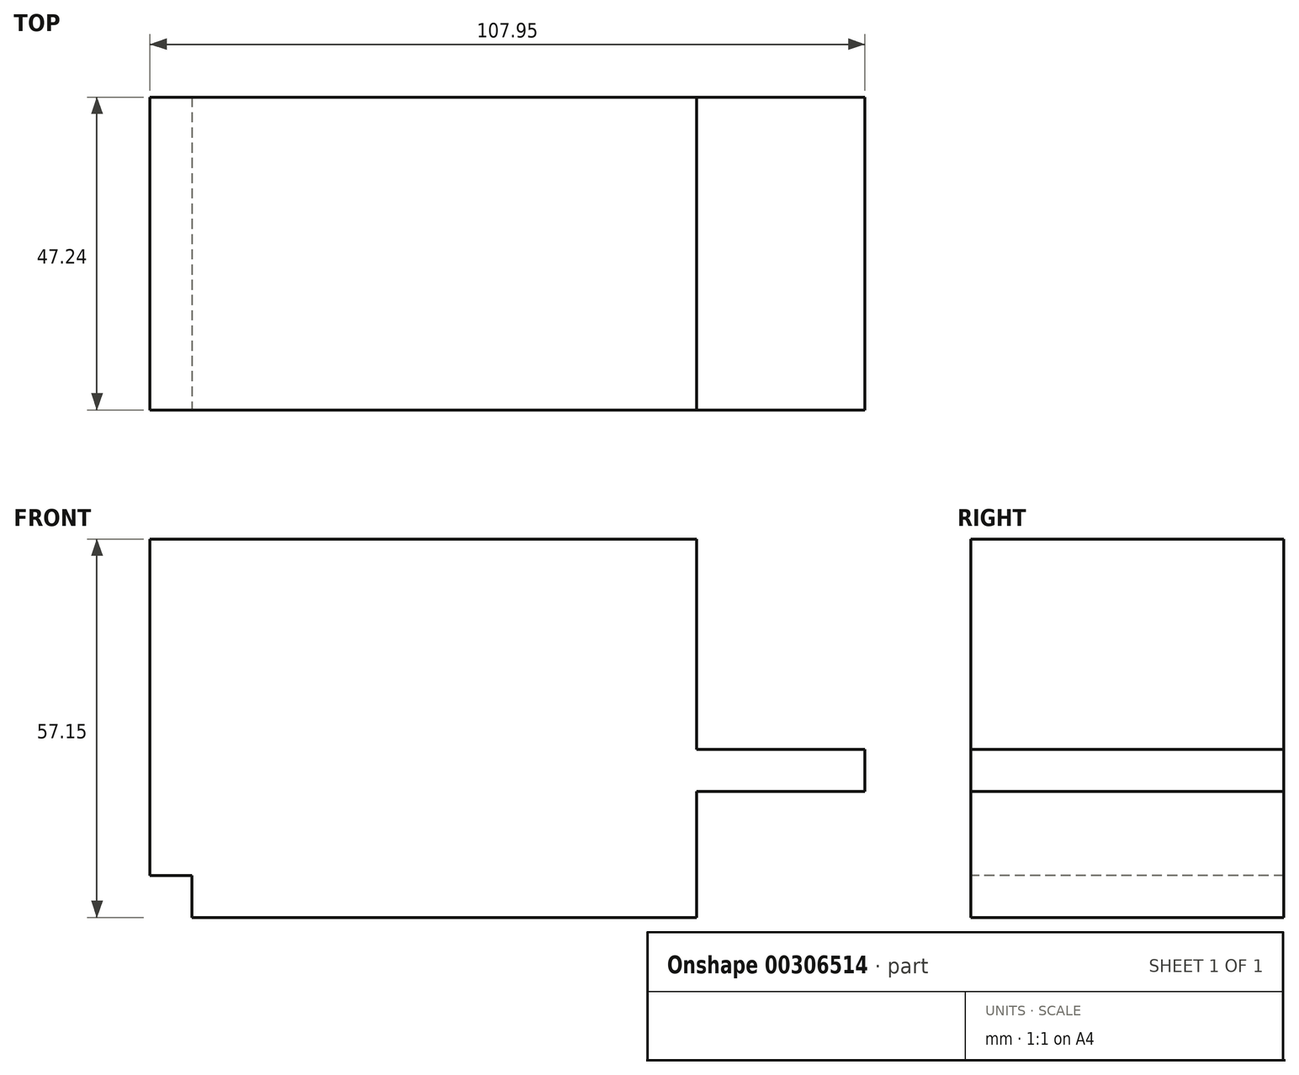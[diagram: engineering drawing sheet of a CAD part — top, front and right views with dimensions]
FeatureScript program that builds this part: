
annotation { "Feature Type Name" : "Feature", "Feature Type Description" : "" }
export const myFeature = defineFeature(function(context is Context, id is Id, definition is map)
    precondition{}
    {
        {
            var Q0;
            Q0=qCreatedBy(makeId("Front.planeOp"),FACE);
            var sketch = newSketch(context, id + "F0", { "sketchPlane" : qUnion([Q0])});
            skLineSegment(sketch, "E0", {"start": v(-29.7, 44.45) * mm, "end": v(-29.7, -6.35) * mm});
            skLineSegment(sketch, "E1", {"start": v(-29.7, -6.35) * mm, "end": v(-23.35, -6.35) * mm});
            skLineSegment(sketch, "E2", {"start": v(-23.35, -6.35) * mm, "end": v(-23.35, -12.7) * mm});
            skLineSegment(sketch, "E3", {"start": v(-23.35, -12.7) * mm, "end": v(52.85, -12.7) * mm});
            skLineSegment(sketch, "E4", {"start": v(52.85, -12.7) * mm, "end": v(52.85, 6.35) * mm});
            skLineSegment(sketch, "E5", {"start": v(52.85, 6.35) * mm, "end": v(78.25, 6.35) * mm});
            skLineSegment(sketch, "E6", {"start": v(78.25, 6.35) * mm, "end": v(78.25, 12.7) * mm});
            skLineSegment(sketch, "E7", {"start": v(78.25, 12.7) * mm, "end": v(52.85, 12.7) * mm});
            skLineSegment(sketch, "E8", {"start": v(52.85, 12.7) * mm, "end": v(52.85, 44.45) * mm});
            skLineSegment(sketch, "E9", {"start": v(52.85, 44.45) * mm, "end": v(-29.7, 44.45) * mm});
            skSolve(sketch);
        }
        {
            var Q0;
            Q0=makeQuery(id+"F0.imprint","IMPRINT",FACE,{"disambiguationData":[TD([[makeQuery(id+"F0.imprint","IMPRINT",EDGE,{"derivedFrom":sQuery(id+"F0.wireOp",EDGE,"E0")}),1.0]])]});
            extrude(context, id + "F1", {"entities" : qUnion([Q0]), "depth" : 25.4 * mm});
        }
        {
            var Q0;
            Q0=makeQuery(id+"F1.opExtrude","CAP_FACE",FACE,{"disambiguationData":[OSD([sQuery(id+"F0.wireOp",EDGE,"E0"),sQuery(id+"F0.wireOp",EDGE,"E1"),sQuery(id+"F0.wireOp",EDGE,"E2"),sQuery(id+"F0.wireOp",EDGE,"E3"),sQuery(id+"F0.wireOp",EDGE,"E4"),sQuery(id+"F0.wireOp",EDGE,"E5"),sQuery(id+"F0.wireOp",EDGE,"E6"),sQuery(id+"F0.wireOp",EDGE,"E7"),sQuery(id+"F0.wireOp",EDGE,"E8"),sQuery(id+"F0.wireOp",EDGE,"E9")])],"isStart":true});
            extrude(context, id + "F2", {"entities" : qUnion([Q0]), "operationType" : NewBodyOperationType.ADD, "depth" : 25.4 * mm});
        }
        {
            var Q0;
            Q0=makeQuery(id+"F1.opExtrude","CAP_FACE",FACE,{"disambiguationData":[OSD([sQuery(id+"F0.wireOp",EDGE,"E0"),sQuery(id+"F0.wireOp",EDGE,"E1"),sQuery(id+"F0.wireOp",EDGE,"E2"),sQuery(id+"F0.wireOp",EDGE,"E3"),sQuery(id+"F0.wireOp",EDGE,"E4"),sQuery(id+"F0.wireOp",EDGE,"E5"),sQuery(id+"F0.wireOp",EDGE,"E6"),sQuery(id+"F0.wireOp",EDGE,"E7"),sQuery(id+"F0.wireOp",EDGE,"E8"),sQuery(id+"F0.wireOp",EDGE,"E9")])],"isStart":false});
            var sketch = newSketch(context, id + "F3", { "sketchPlane" : qUnion([Q0])});
            skLineSegment(sketch, "E10", {"start": v(-29.7, 44.45) * mm, "end": v(-29.7, 107.95) * mm});
            skLineSegment(sketch, "E11", {"start": v(-29.7, 107.95) * mm, "end": v(65.55, 107.95) * mm});
            skLineSegment(sketch, "E12", {"start": v(52.85, -12.7) * mm, "end": v(154.45, -12.7) * mm});
            skLineSegment(sketch, "E13", {"start": v(154.45, -12.7) * mm, "end": v(154.45, 25.4) * mm});
            skLineSegment(sketch, "E14", {"start": v(65.55, 107.95) * mm, "end": v(154.45, 25.4) * mm});
            skSolve(sketch);
        }
        {
            var Q0;
            Q0=makeQuery(id+"F3.imprint","IMPRINT",FACE,{"disambiguationData":[TD([[makeQuery(id+"F3.imprint","IMPRINT",EDGE,{"derivedFrom":sQuery(id+"F3.wireOp",EDGE,"E10")}),-1.0]])]});
            extrude(context, id + "F4", {"entities" : qUnion([Q0]), "operationType" : NewBodyOperationType.ADD, "oppositeDirection" : true, "depth" : 88.65 * mm});
        }
        {
            var Q0;
            {var subQ0=sQuery(id+"F0.wireOp",EDGE,"E9");var subQ1=sQuery(id+"F0.wireOp",EDGE,"E8");var subQ2=sQuery(id+"F0.wireOp",EDGE,"E7");var subQ3=sQuery(id+"F0.wireOp",EDGE,"E6");var subQ4=sQuery(id+"F0.wireOp",EDGE,"E5");var subQ5=sQuery(id+"F0.wireOp",EDGE,"E4");Q0=makeQuery(id+"F4.boolean.opBoolean","MERGE",FACE,{"derivedFrom":[makeQuery(id+"F1.opExtrude","CAP_FACE",FACE,{"disambiguationData":[OSD([sQuery(id+"F0.wireOp",EDGE,"E0"),sQuery(id+"F0.wireOp",EDGE,"E1"),sQuery(id+"F0.wireOp",EDGE,"E2"),sQuery(id+"F0.wireOp",EDGE,"E3"),subQ5,subQ4,subQ3,subQ2,subQ1,subQ0])],"isStart":false}),makeQuery(id+"F4.opExtrude","CAP_FACE",FACE,{"disambiguationData":[OSD([subQ5,subQ4,subQ3,subQ2,subQ1,subQ0,sQuery(id+"F3.wireOp",EDGE,"E10"),sQuery(id+"F3.wireOp",EDGE,"E11"),sQuery(id+"F3.wireOp",EDGE,"E12"),sQuery(id+"F3.wireOp",EDGE,"E13"),sQuery(id+"F3.wireOp",EDGE,"E14")])],"isStart":true})]});}
            extrude(context, id + "F5", {"entities" : qUnion([Q0]), "operationType" : NewBodyOperationType.REMOVE, "oppositeDirection" : true, "depth" : 89.92 * mm});
        }
        {
            var Q0;
            Q0=makeQuery(id+"F0.imprint","IMPRINT",FACE,{"disambiguationData":[TD([[makeQuery(id+"F0.imprint","IMPRINT",EDGE,{"derivedFrom":sQuery(id+"F0.wireOp",EDGE,"E0")}),1.0]])]});
            extrude(context, id + "F6", {"entities" : qUnion([Q0]), "oppositeDirection" : true, "depth" : 47.24 * mm});
        }
    });
